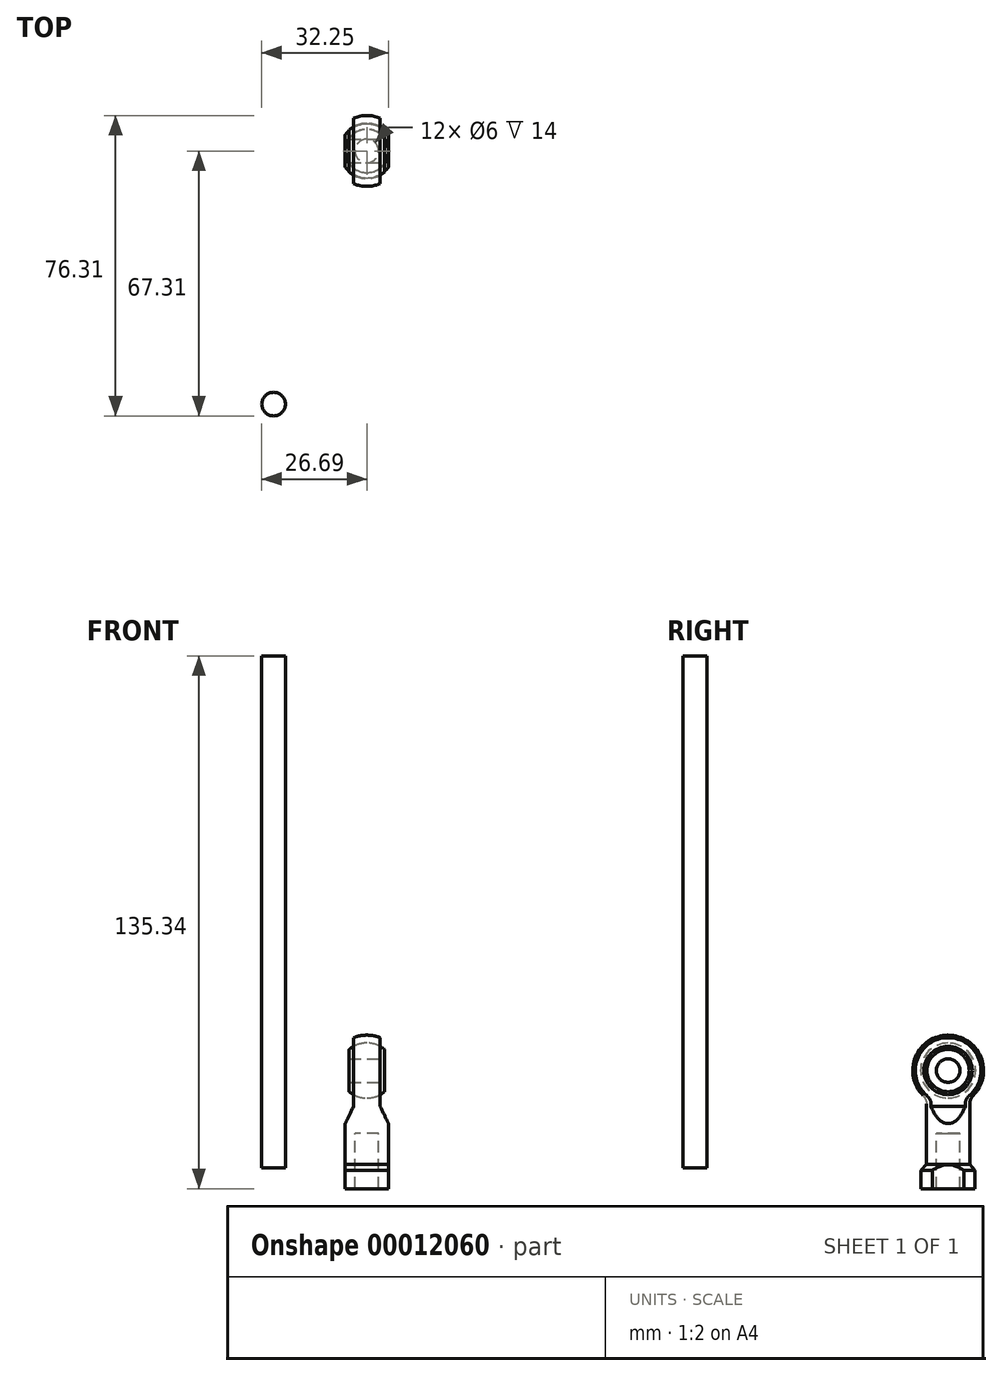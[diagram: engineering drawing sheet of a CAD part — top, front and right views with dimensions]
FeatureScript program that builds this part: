
annotation { "Feature Type Name" : "Feature", "Feature Type Description" : "" }
export const myFeature = defineFeature(function(context is Context, id is Id, definition is map)
    precondition{}
    {
        {
            var Q0;
            Q0=qCreatedBy(makeId("Front.planeOp"),FACE);
            var sketch = newSketch(context, id + "F0", { "sketchPlane" : qUnion([Q0])});
            skLineSegment(sketch, "E0", {"start": v(3, -5.34) * mm, "end": v(6.85, -5.34) * mm});
            skLineSegment(sketch, "E1", {"start": v(6.85, -5.34) * mm, "end": v(6.85, -0.64) * mm});
            skLineSegment(sketch, "E2", {"start": v(6.85, -0.64) * mm, "end": v(5.5, 0.8) * mm});
            skLineSegment(sketch, "E3", {"start": v(5.5, 0.8) * mm, "end": v(5.5, 17.54) * mm});
            skArc(sketch, "E4", {"start": v(5.5, 17.54) * mm, "mid": v(8.52, 27.57) * mm, "end": v(0, 33.66) * mm});
            skLineSegment(sketch, "E5", {"start": v(0, 33.66) * mm, "end": v(0, 8.66) * mm});
            skLineSegment(sketch, "E6", {"start": v(0, 8.66) * mm, "end": v(3, 8.66) * mm});
            skLineSegment(sketch, "E7", {"start": v(3, 8.66) * mm, "end": v(3, -5.34) * mm});
            skPoint(sketch, "E8.orphan", {"position": v(0, -5.34) * mm});
            skSolve(sketch);
        }
        {
            var Q0;
            Q0=makeQuery(id+"F0.imprint","IMPRINT",FACE,{"disambiguationData":[TD([[makeQuery(id+"F0.imprint","IMPRINT",EDGE,{"derivedFrom":sQuery(id+"F0.wireOp",EDGE,"E0")}),1.0]])]});
            var Q1;
            Q1=sQuery(id+"F0.wireOp",EDGE,"E5");
            revolve(context, id + "F1", {"entities" : qUnion([Q0]), "axis" : qUnion([Q1]), "revolveType" : RevolveType.FULL});
        }
        {
            var Q0;
            Q0=qCreatedBy(makeId("Front.planeOp"),FACE);
            var sketch = newSketch(context, id + "F2", { "sketchPlane" : qUnion([Q0])});
            skLineSegment(sketch, "E9", {"start": v(3.38, 34.79) * mm, "end": v(3.38, 15.56) * mm});
            skLineSegment(sketch, "E10", {"start": v(3.38, 15.56) * mm, "end": v(5.56, 11.07) * mm});
            skLineSegment(sketch, "E11", {"start": v(5.56, 11.07) * mm, "end": v(5.56, -7.8) * mm});
            skLineSegment(sketch, "E12", {"start": v(5.56, -7.8) * mm, "end": v(18.45, -7.8) * mm});
            skLineSegment(sketch, "E13", {"start": v(18.45, -7.8) * mm, "end": v(18.45, 34.79) * mm});
            skLineSegment(sketch, "E14", {"start": v(18.45, 34.79) * mm, "end": v(3.37, 34.79) * mm});
            skSolve(sketch);
        }
        {
            var Q0;
            Q0=qSketchRegion(id+"F2",true);
            extrude(context, id + "F3", {"entities" : qUnion([Q0]), "endBound" : BoundingType.SYMMETRIC, "depth" : 50 * mm});
        }
        {
            var Q0;
            Q0=makeQuery(id+"F3.opExtrude","SWEPT_BODY",BODY,{"disambiguationData":[OSD([sQuery(id+"F2.wireOp",EDGE,"E9"),sQuery(id+"F2.wireOp",EDGE,"E10"),sQuery(id+"F2.wireOp",EDGE,"E11"),sQuery(id+"F2.wireOp",EDGE,"E12"),sQuery(id+"F2.wireOp",EDGE,"E13"),sQuery(id+"F2.wireOp",EDGE,"E14")])]});
            var Q1;
            Q1=qCreatedBy(makeId("Right.planeOp"),FACE);
            mirror(context, id + "F4", {"entities" : qUnion([Q0]), "mirrorPlane" : qUnion([Q1])});
        }
        {
            var Q0;
            Q0=makeQuery(id+"F4.opPattern","COPY",BODY,{"derivedFrom":makeQuery(id+"F3.opExtrude","SWEPT_BODY",BODY,{"disambiguationData":[OSD([sQuery(id+"F2.wireOp",EDGE,"E9"),sQuery(id+"F2.wireOp",EDGE,"E10"),sQuery(id+"F2.wireOp",EDGE,"E11"),sQuery(id+"F2.wireOp",EDGE,"E12"),sQuery(id+"F2.wireOp",EDGE,"E13"),sQuery(id+"F2.wireOp",EDGE,"E14")])]}),"instanceName":"1"});
            var Q1;
            Q1=makeQuery(id+"F3.opExtrude","SWEPT_BODY",BODY,{"disambiguationData":[OSD([sQuery(id+"F2.wireOp",EDGE,"E9"),sQuery(id+"F2.wireOp",EDGE,"E10"),sQuery(id+"F2.wireOp",EDGE,"E11"),sQuery(id+"F2.wireOp",EDGE,"E12"),sQuery(id+"F2.wireOp",EDGE,"E13"),sQuery(id+"F2.wireOp",EDGE,"E14")])]});
            var Q2;
            Q2=makeQuery(id+"F1.opRevolve","SWEPT_BODY",BODY,{"disambiguationData":[OSD([sQuery(id+"F0.wireOp",EDGE,"E0"),sQuery(id+"F0.wireOp",EDGE,"E1"),sQuery(id+"F0.wireOp",EDGE,"E2"),sQuery(id+"F0.wireOp",EDGE,"E3"),sQuery(id+"F0.wireOp",EDGE,"E4"),sQuery(id+"F0.wireOp",EDGE,"E5")])]});
            booleanBodies(context, id + "F5", {"operationType" : BooleanOperationType.SUBTRACTION, "tools" : qUnion([Q0, Q1]), "targets" : qUnion([Q2])});
        }
        {
            var Q0;
            Q0=makeQuery(id+"F5.opBoolean","SPLIT",EDGE,{"disambiguationData":[OD(0.0)],"derivedFrom":makeQuery(id+"F1.opRevolve","SWEPT_EDGE",EDGE,{"disambiguationData":[OSD([sQuery(id+"F0.wireOp",EDGE,"E3"),sQuery(id+"F0.wireOp",EDGE,"E4")])]})});
            var Q1;
            Q1=makeQuery(id+"F5.opBoolean","SPLIT",EDGE,{"disambiguationData":[OD(1.0)],"derivedFrom":makeQuery(id+"F1.opRevolve","SWEPT_EDGE",EDGE,{"disambiguationData":[OSD([sQuery(id+"F0.wireOp",EDGE,"E3"),sQuery(id+"F0.wireOp",EDGE,"E4")])]})});
            fillet(context, id + "F6", {"entities" : qUnion([Q0, Q1]), "radius" : 3 * mm, "tangentPropagation" : true, "allowEdgeOverflow" : false});
        }
        {
            var Q0;
            Q0=qCreatedBy(makeId("Right.planeOp"),FACE);
            var sketch = newSketch(context, id + "F7", { "sketchPlane" : qUnion([Q0])});
            skArc(sketch, "E15.0", {"start": v(5.4, 18.31) * mm, "mid": v(0, 33) * mm, "end": v(-5.4, 18.31) * mm});
            skArc(sketch, "E16", {"start": v(0, 17.66) * mm, "mid": v(7, 24.66) * mm, "end": v(0, 31.66) * mm});
            skLineSegment(sketch, "E17", {"start": v(0, 31.66) * mm, "end": v(0, 17.66) * mm});
            skSolve(sketch);
        }
        {
            var Q0;
            Q0=qSketchRegion(id+"F7",true);
            var Q1;
            Q1=sQuery(id+"F7.wireOp",EDGE,"E17");
            revolve(context, id + "F8", {"entities" : qUnion([Q0]), "axis" : qUnion([Q1]), "revolveType" : RevolveType.FULL});
        }
        {
            var Q0;
            Q0=makeQuery(id+"F8.opRevolve","SWEPT_BODY",BODY,{"disambiguationData":[OSD([sQuery(id+"F7.wireOp",EDGE,"E16"),sQuery(id+"F7.wireOp",EDGE,"E17")])]});
            transform(context, id + "F9", {"entities" : qUnion([Q0]), "transformType" : TransformType.TRANSLATION_3D, "dx" : 0 * mm, "dy" : 0 * mm, "dz" : 0 * mm, "makeCopy" : true});
        }
        {
            var Q0;
            Q0=makeQuery(id+"F8.opRevolve","SWEPT_BODY",BODY,{"disambiguationData":[OSD([sQuery(id+"F7.wireOp",EDGE,"E16"),sQuery(id+"F7.wireOp",EDGE,"E17")])]});
            var Q1;
            Q1=makeQuery(id+"F1.opRevolve","SWEPT_BODY",BODY,{"disambiguationData":[OSD([sQuery(id+"F0.wireOp",EDGE,"E0"),sQuery(id+"F0.wireOp",EDGE,"E1"),sQuery(id+"F0.wireOp",EDGE,"E2"),sQuery(id+"F0.wireOp",EDGE,"E3"),sQuery(id+"F0.wireOp",EDGE,"E4"),sQuery(id+"F0.wireOp",EDGE,"E5")])]});
            booleanBodies(context, id + "F10", {"operationType" : BooleanOperationType.SUBTRACTION, "tools" : qUnion([Q0]), "targets" : qUnion([Q1])});
        }
        {
            var Q0;
            Q0=qCreatedBy(makeId("Front.planeOp"),FACE);
            var sketch = newSketch(context, id + "F11", { "sketchPlane" : qUnion([Q0])});
            skLineSegment(sketch, "E18.bottom", {"start": v(4.5, 32.4) * mm, "end": v(14.9, 32.4) * mm});
            skLineSegment(sketch, "E18.top", {"start": v(4.5, 17.86) * mm, "end": v(14.9, 17.86) * mm});
            skLineSegment(sketch, "E18.left", {"start": v(4.5, 32.4) * mm, "end": v(4.5, 17.86) * mm});
            skLineSegment(sketch, "E18.right", {"start": v(14.9, 32.4) * mm, "end": v(14.9, 17.86) * mm});
            skSolve(sketch);
        }
        {
            var Q0;
            Q0=qSketchRegion(id+"F11",true);
            extrude(context, id + "F12", {"entities" : qUnion([Q0]), "endBound" : BoundingType.SYMMETRIC, "depth" : 50 * mm});
        }
        {
            var Q0;
            Q0=makeQuery(id+"F12.opExtrude","SWEPT_BODY",BODY,{"disambiguationData":[OSD([sQuery(id+"F11.wireOp",EDGE,"E18.bottom"),sQuery(id+"F11.wireOp",EDGE,"E18.top"),sQuery(id+"F11.wireOp",EDGE,"E18.left"),sQuery(id+"F11.wireOp",EDGE,"E18.right")])]});
            var Q1;
            Q1=qCreatedBy(makeId("Right.planeOp"),FACE);
            mirror(context, id + "F13", {"entities" : qUnion([Q0]), "mirrorPlane" : qUnion([Q1])});
        }
        {
            var Q0;
            Q0=makeQuery(id+"F13.opPattern","COPY",BODY,{"derivedFrom":makeQuery(id+"F12.opExtrude","SWEPT_BODY",BODY,{"disambiguationData":[OSD([sQuery(id+"F11.wireOp",EDGE,"E18.bottom"),sQuery(id+"F11.wireOp",EDGE,"E18.top"),sQuery(id+"F11.wireOp",EDGE,"E18.left"),sQuery(id+"F11.wireOp",EDGE,"E18.right")])]}),"instanceName":"1"});
            var Q1;
            Q1=makeQuery(id+"F12.opExtrude","SWEPT_BODY",BODY,{"disambiguationData":[OSD([sQuery(id+"F11.wireOp",EDGE,"E18.bottom"),sQuery(id+"F11.wireOp",EDGE,"E18.top"),sQuery(id+"F11.wireOp",EDGE,"E18.left"),sQuery(id+"F11.wireOp",EDGE,"E18.right")])]});
            var Q2;
            Q2=makeQuery(id+"F9.opPattern","COPY",BODY,{"derivedFrom":makeQuery(id+"F8.opRevolve","SWEPT_BODY",BODY,{"disambiguationData":[OSD([sQuery(id+"F7.wireOp",EDGE,"E16"),sQuery(id+"F7.wireOp",EDGE,"E17")])]}),"instanceName":"1"});
            booleanBodies(context, id + "F14", {"operationType" : BooleanOperationType.SUBTRACTION, "tools" : qUnion([Q0, Q1]), "targets" : qUnion([Q2])});
        }
        {
            var Q0;
            Q0=makeQuery(id+"F14.opBoolean","COPY",FACE,{"derivedFrom":makeQuery(id+"F12.opExtrude","SWEPT_FACE",FACE,{"disambiguationData":[OSD([sQuery(id+"F11.wireOp",EDGE,"E18.left")])]})});
            var sketch = newSketch(context, id + "F15", { "sketchPlane" : qUnion([Q0])});
            skCircle(sketch, "E19", {"center": v(0, 24.66) * mm, "radius": 3 * mm});
            skSolve(sketch);
        }
        {
            var Q0;
            Q0=makeQuery(id+"F15.imprint","IMPRINT",FACE,{"disambiguationData":[TD([[makeQuery(id+"F15.imprint","IMPRINT",EDGE,{"derivedFrom":sQuery(id+"F15.wireOp",EDGE,"E19")}),1.0]])]});
            extrude(context, id + "F16", {"entities" : qUnion([Q0]), "operationType" : NewBodyOperationType.REMOVE, "endBound" : BoundingType.THROUGH_ALL, "oppositeDirection" : true, "depth" : 25 * mm});
        }
        {
            var Q0;
            Q0=qCreatedBy(makeId("Top.planeOp"),FACE);
            var sketch = newSketch(context, id + "F17", { "sketchPlane" : qUnion([Q0])});
            skCircle(sketch, "E20", {"center": v(-23.69, -64.31) * mm, "radius": 3 * mm});
            skSolve(sketch);
        }
        {
            var Q0;
            Q0=makeQuery(id+"F17.imprint","IMPRINT",FACE,{"disambiguationData":[TD([[makeQuery(id+"F17.imprint","IMPRINT",EDGE,{"derivedFrom":sQuery(id+"F17.wireOp",EDGE,"E20")}),1.0]])]});
            extrude(context, id + "F18", {"entities" : qUnion([Q0]), "depth" : 130 * mm});
        }
    });
